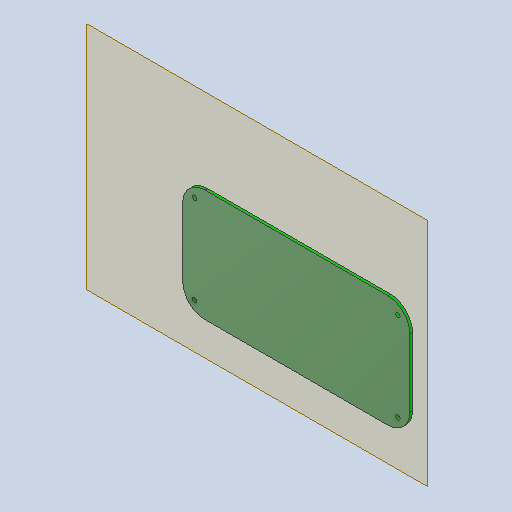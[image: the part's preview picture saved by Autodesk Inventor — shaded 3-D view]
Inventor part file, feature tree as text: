
AUTODESK INVENTOR PART (.ipt)
format: ipt  version: 2024.2 (Build 282272000, 272)  size: 148,992 bytes
history: native  units: mm
features: other x5, extrude x1, sketch x1
ambient origin geometry x8: Origin, YZ Plane, XZ Plane, XY Plane, X Axis, Y Axis, Z Axis, Center Point
bodies: Body1 (feature_tree)
feature tree (7):
  other  "Твердое тело1"
  other  "РабПлоскость1"
  extrude  "Выдавливание1"  Depth=15.0mm
  sketch  "Эскиз1"
  other  "<userpath>\Documents\Artist-v2\3D\Робот.iam"
  other  "Робот.iam"
  other  "крышка:1"
